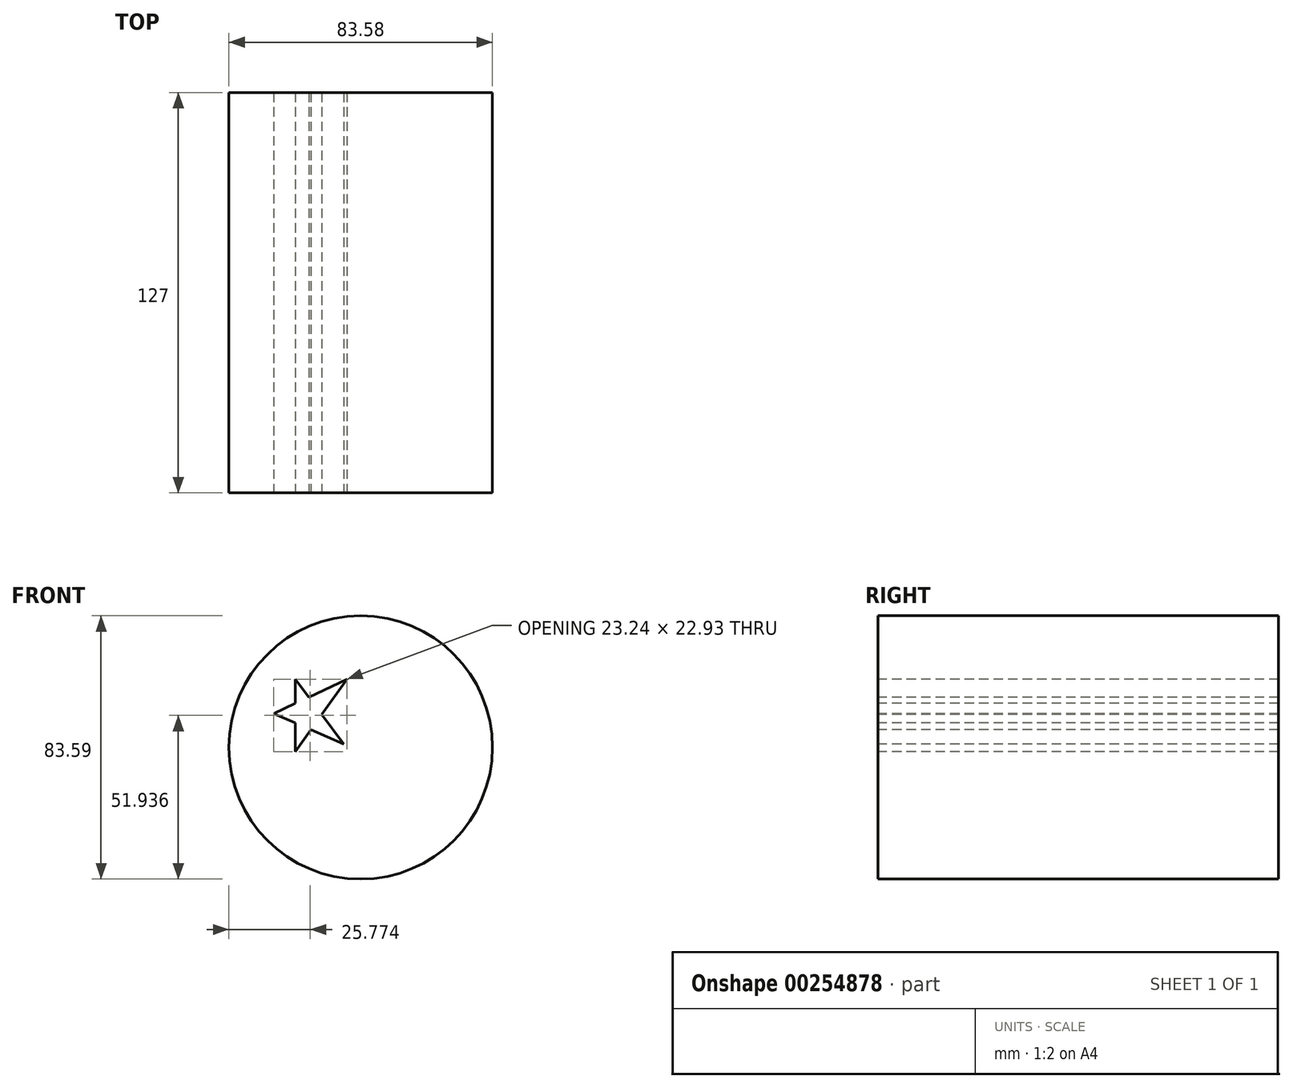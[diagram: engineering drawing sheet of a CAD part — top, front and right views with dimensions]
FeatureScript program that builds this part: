
annotation { "Feature Type Name" : "Feature", "Feature Type Description" : "" }
export const myFeature = defineFeature(function(context is Context, id is Id, definition is map)
    precondition{}
    {
        {
            var Q0;
            Q0=qCreatedBy(makeId("Front.planeOp"),FACE);
            var sketch = newSketch(context, id + "F0", { "sketchPlane" : qUnion([Q0])});
            skCircle(sketch, "E0", {"center": v(-9.81, 15.38) * mm, "radius": 41.8 * mm});
            skPoint(sketch, "E0.first.point", {"position": v(-41.68, 42.4) * mm});
            skPoint(sketch, "E0.second.point", {"position": v(28.56, 31.92) * mm});
            skPoint(sketch, "E0.third.point", {"position": v(-24.48, -23.76) * mm});
            skSolve(sketch);
        }
        {
            var Q0;
            Q0 = qSketchRegion(id + "F0", true);
            extrude(context, id + "F1", {"entities" : qUnion([Q0]), "endBound" : BoundingType.SYMMETRIC, "depth" : 127 * mm});
        }
        {
            var Q0;
            Q0=makeQuery(id+"F1.opExtrude","CAP_FACE",FACE,{"disambiguationData":[OSD([sQuery(id+"F0.wireOp",EDGE,"E0")])],"isStart":false});
            var sketch = newSketch(context, id + "F2", { "sketchPlane" : qUnion([Q0])});
            skLineSegment(sketch, "E1", {"start": v(-15.11, 16.46) * mm, "end": v(-37.44, 26.12) * mm});
            skLineSegment(sketch, "E2", {"start": v(-37.44, 26.12) * mm, "end": v(-14.2, 36.98) * mm});
            skLineSegment(sketch, "E3", {"start": v(-14.2, 36.98) * mm, "end": v(-30.5, 14.05) * mm});
            skLineSegment(sketch, "E4", {"start": v(-30.5, 14.05) * mm, "end": v(-30.5, 36.98) * mm});
            skLineSegment(sketch, "E5", {"start": v(-30.5, 36.98) * mm, "end": v(-15.11, 16.46) * mm});
            skSolve(sketch);
        }
        {
            var Q0;
            Q0 = qSketchRegion(id + "F2", true);
            extrude(context, id + "F3", {"entities" : qUnion([Q0]), "operationType" : NewBodyOperationType.REMOVE, "endBound" : BoundingType.THROUGH_ALL, "oppositeDirection" : true, "depth" : 25.4 * mm});
        }
    });
